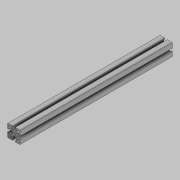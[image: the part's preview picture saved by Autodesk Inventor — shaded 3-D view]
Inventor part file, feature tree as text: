
AUTODESK INVENTOR PART (.ipt)
format: ipt  version: 2021.2 (Build 252289000, 289)  size: 202,752 bytes
history: native  units: in
note: dims shown in document units (in); Inventor stores cm internally (conversion verified against a paired STEP export)
features: other x2, extrude x1, sketch x1, projected_geometry x1
ambient origin geometry x8: Origin, YZ Plane, XZ Plane, XY Plane, X Axis, Y Axis, Z Axis, Center Point
bodies: Body1 (feature_tree)
feature tree (5):
  other  "ソリッド2"
  extrude  "押し出し1"  Depth=14.1732in
  sketch  "スケッチ2"
  projected_geometry  "投影ループ1"
  other  "ソリッド1"
